# Revit family: Condensing-Storage-Water-Heater-Gas_AO_Smith-BFC_28_PF
name_source: partatom
category: Mechanical Equipment
revit_build: Autodesk Revit 2014 (Build: 20130308_1515(x64)
units: mm (PartAtom-declared; Revit-internal decimal feet)

## types (1)
- Condensing-Storage-Water-Heater-Gas_AO_Smith-BFC_28_PF
    (Contrôle supplémentaires) Fréquence secteur (± 1 Hz) = 0 Hz
    (Contrôle supplémentaires) Phase = 1
    (Contrôle supplémentaires) Puissance Électrique Absorbée = 0 W
    (Contrôle supplémentaires) Tension d'Alimentation (-15%, +10%) = 0 V
    1er Entretien (check-up) = 3 mois après l'installation
    2ème Entretien (Entretien Général) = 12 mois après l'installation
    Assembly Code = D3010
    BIM Content Developer = CAD & Company
    CE-PIN = 0063BU3889
    CO2-émissions (tol. ± 1.0) = 10.0
    Capacité = 217.0 L
    Catégorie de Gaz = II2Esi3P
    Charge Maximale au Sol = 394 kg
    Charge Nominale (Valeur Inférieure) = 29000 W
    Charge Nominale (Valeur Supérieure) = 31500 W
    Consommation de Gaz - Masse = 2.3
    Consommation de Gaz - Volume = 0
    Description = Générateur Gaz ECS à Condensation Haut Rendement
    Destination / Pays = France
    Diamètre = 705 mm
    Diamètre Cheminée - Boiler = 100/150 mm/mm
    Diamètre Cheminée - Système Concentrique = 100/150 mm/mm
    Diamètre Cheminée - Système Parallèle = 100 mm  [stored 0.328084 ft]
    Débit de vidage en Continu à ΔT = 28°C = 960.0 L/s
    Débit de vidage en Continu à ΔT = 44°C = 610.0 L/s
    Débit de vidage en Continu à ΔT = 50°C = 540.0 L/s
    Débit de vidage en Continu à ΔT = 55°C = 490.0 L/s
    Débit de vidage en Continu à ΔT = 70°C = 390.0 L/s
    Débit de vidage à ΔT = 28°C après 120 min. = 2200.0 L
    Débit de vidage à ΔT = 28°C après 30 min. = 730.0 L
    Débit de vidage à ΔT = 28°C après 60 min. = 1300.0 L
    Débit de vidage à ΔT = 28°C après 90 min. = 1700.0 L
    Débit de vidage à ΔT = 44°C après 120 min. = 1400.0 L
    Débit de vidage à ΔT = 44°C après 30 min. = 430.0 L
    Débit de vidage à ΔT = 44°C après 60 min. = 730.0 L
    Débit de vidage à ΔT = 44°C après 90 min. = 1100.0 L
    Débit de vidage à ΔT = 50°C après 120 min. = 1200.0 L
    Débit de vidage à ΔT = 50°C après 30 min. = 360.0 L
    Débit de vidage à ΔT = 50°C après 60 min. = 630.0 L
    Débit de vidage à ΔT = 50°C après 90 min. = 900.0 L
    Débit de vidage à ΔT = 55°C après 120 min. = 1100.0 L
    Débit de vidage à ΔT = 55°C après 30 min. = 320.0 L
    Débit de vidage à ΔT = 55°C après 60 min. = 560.0 L
    Débit de vidage à ΔT = 55°C après 90 min. = 800.0 L
    Débit de vidage à ΔT = 70°C après 120 min. = 790.0 L
    Débit de vidage à ΔT = 70°C après 30 min. = 210.0 L
    Débit de vidage à ΔT = 70°C après 60 min. = 400.0 L
    Débit de vidage à ΔT = 70°C après 90 min. = 600.0 L
    Epaisseur d'Isolation = 50 mm  [stored 0.164042 ft]
    Fabricant No. = E 7110
    Fréquence secteur (± 1 Hz) = 50 Hz
    Garantie Pièces = 12 mois
    Garantie sur la Cuve = 36 mois
    Guide de Produit = https://www.aosmithinternational.com
    Hauteur = 1390 mm  [stored 4.56037 ft]
    Hauteur Conduit d'Alimentation en Air = 1365 mm
    Hauteur Conduit d'Évacuation des Fumées = 1365 mm
    Hauteur d'Emballage = 1550 mm
    Hauteur de l'Alimentation en eau Froide = 170 mm
    Hauteur de la Sortie d'eau Chaude = 1390 mm  [stored 4.56037 ft]
    Hauteur du Raccordement au Gaz = 1285 mm
    Largeur = 0 mm  [stored 0 ft]
    Largeur d'Emballage = 790 mm
    Manufacturer = A.O. Smith Water Products Company b.v.
    Model = BFC 28 PF
    NOX-émissions = 54
    NOX-émissions (ven air, 0% O2) = 30
    Niveau du Son = 45
    Nombre de modèle du produit (EAN) = 8717449113001
    Pertes en Veille = 0 W
    Pertes en Veille - tous les jours (24h) = 0 W
    Phase = 1
    Poids de Transport = 196 kg
    Poids à vide = 177 kg
    Pression Amont de Gaz = 3700
    Pression Différentielle d'Ouverture de l'Interrupteur de Pression = 115.0 Pa
    Pression de Fonctionnement Maximale = 800000.0 Pa
    Production Nominale = 31000 W
    Profondeur = 0 mm  [stored 0 ft]
    Profondeur d'Emballage = 950 mm
    Puissance Électrique Absorbée = 45 W
    Raccord Robinet de Vidange = 1"
    Raccord d'Alimentation en Eau Froide = 1 1/2"
    Raccord de Gaz = 3/4"
    Raccord de Sortie d'Eau Chaude = 1 1/2"
    Raccord de la Soupape de Vidange = 1"
    Raccord Évacuation de la Condensation = 40 mm  [stored 0.131234 ft]
    Rendement (Hi, acc. NEN-EN 89 - 1999) = 107
    Rendement (Hs, acc. NEN-EN 89 - 1999) = 96
    Rendement Saisonnier (Hs) = 96
    Réglage Standard Pour = G31
    Spécifications du Produit = https://www.aosmithinternational.com
    Temps de réchauffement à ΔT = 28°C = 14
    Temps de réchauffement à ΔT = 44°C = 21
    Temps de réchauffement à ΔT = 50°C = 24
    Temps de réchauffement à ΔT = 55°C = 27
    Temps de réchauffement à ΔT = 70°C = 34
    Température Maximale des Fumées = 45 °C
    Tension d'Alimentation (-15%, +10%) = 230 V
    Type d'Emballage = Plastique Emballage Rétractable, Carton et Bois
    Type d'Installation = B23/C13/C33/C43/C53/C63
    URL = http://www.aosmith.fr
    Valeur Défaut du Thermostat de Régulation = 65 °C
    Valeur Manimale du Thermostat de Régulation = 40 °C
    Valeur Maximale du Thermostat de Régulation = 80 °C
    l'Intervalle d'Entretien = 12 mois

note: [stored X ft] marks values corroborated as IEEE doubles in the binary element streams (Revit-internal decimal feet)

## geometry (parser evidence)
native form markers: Blend x23, Sweep x34
no freeform markers — native parametric forms only
